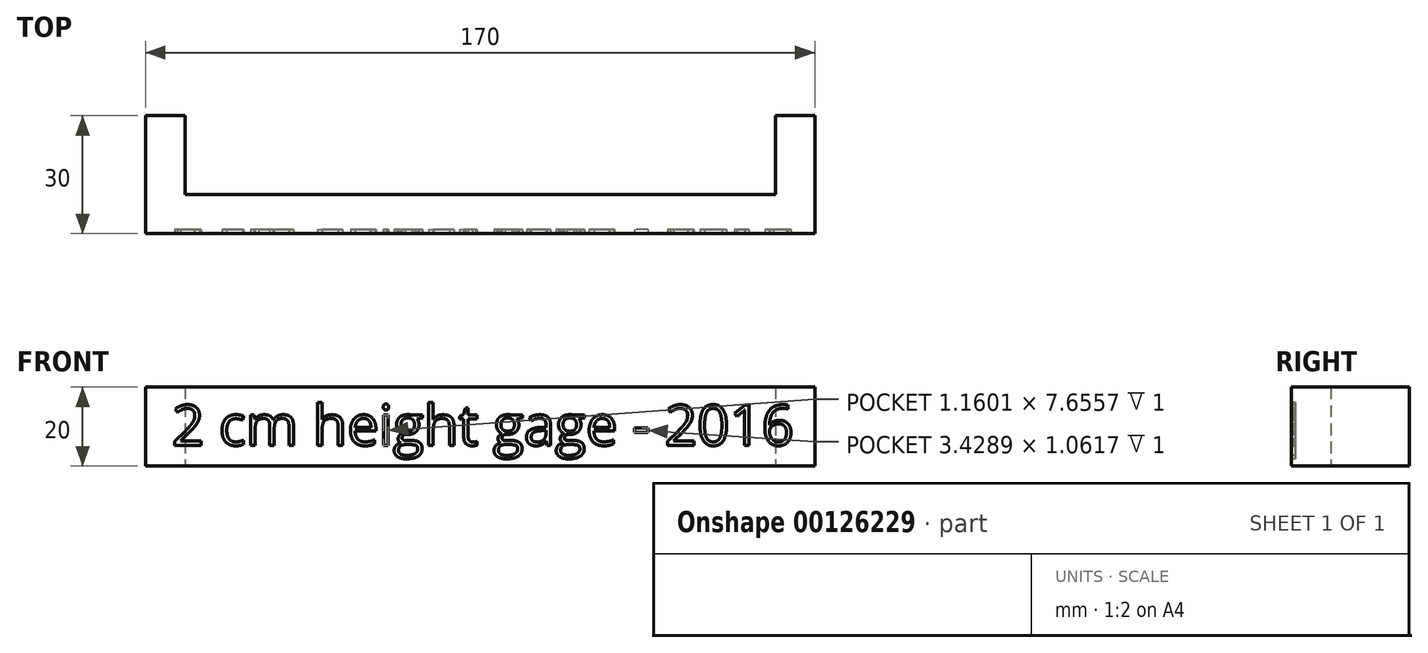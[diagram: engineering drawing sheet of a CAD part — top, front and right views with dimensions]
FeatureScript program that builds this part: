
annotation { "Feature Type Name" : "Feature", "Feature Type Description" : "" }
export const myFeature = defineFeature(function(context is Context, id is Id, definition is map)
    precondition{}
    {
        {
            var Q0;
            Q0=qCreatedBy(makeId("Top.planeOp"),FACE);
            var sketch = newSketch(context, id + "F0", { "sketchPlane" : qUnion([Q0])});
            skLineSegment(sketch, "E0", {"start": v(0, 30) * mm, "end": v(0, 0) * mm});
            skLineSegment(sketch, "E1", {"start": v(0, 0) * mm, "end": v(170, 0) * mm});
            skLineSegment(sketch, "E2", {"start": v(170, 0) * mm, "end": v(170, 30) * mm});
            skLineSegment(sketch, "E3", {"start": v(170, 30) * mm, "end": v(160, 30) * mm});
            skLineSegment(sketch, "E4", {"start": v(160, 30) * mm, "end": v(160, 10) * mm});
            skLineSegment(sketch, "E5", {"start": v(160, 10) * mm, "end": v(10, 10) * mm});
            skLineSegment(sketch, "E6", {"start": v(10, 10) * mm, "end": v(10, 30) * mm});
            skLineSegment(sketch, "E7", {"start": v(10, 30) * mm, "end": v(0, 30) * mm});
            skSolve(sketch);
        }
        {
            var Q0;
            Q0=makeQuery(id+"F0.imprint","IMPRINT",FACE,{"disambiguationData":[TD([[makeQuery(id+"F0.imprint","IMPRINT",EDGE,{"derivedFrom":sQuery(id+"F0.wireOp",EDGE,"E0")}),1.0]])]});
            extrude(context, id + "F1", {"entities" : qUnion([Q0]), "depth" : 20 * mm});
        }
        {
            var Q0;
            Q0=makeQuery(id+"F1.opExtrude","SWEPT_FACE",FACE,{"disambiguationData":[OSD([sQuery(id+"F0.wireOp",EDGE,"E1")])]});
            var sketch = newSketch(context, id + "F2", { "sketchPlane" : qUnion([Q0])});
            skText(sketch, "E8", { "text": "2 cm height gage - 2016", "fontName": "OpenSans-Regular.ttf"});
            const initialGuessF2  = {"E8": [0.00672, 0.00523, 1, 0, 0.0103]};
            skSetInitialGuess(sketch, initialGuessF2);
            skSolve(sketch);
        }
        {
            var Q0;
            Q0 = qSketchRegion(id + "F2", true);
            extrude(context, id + "F3", {"entities" : qUnion([Q0]), "operationType" : NewBodyOperationType.REMOVE, "oppositeDirection" : true, "depth" : 1 * mm});
        }
    });
